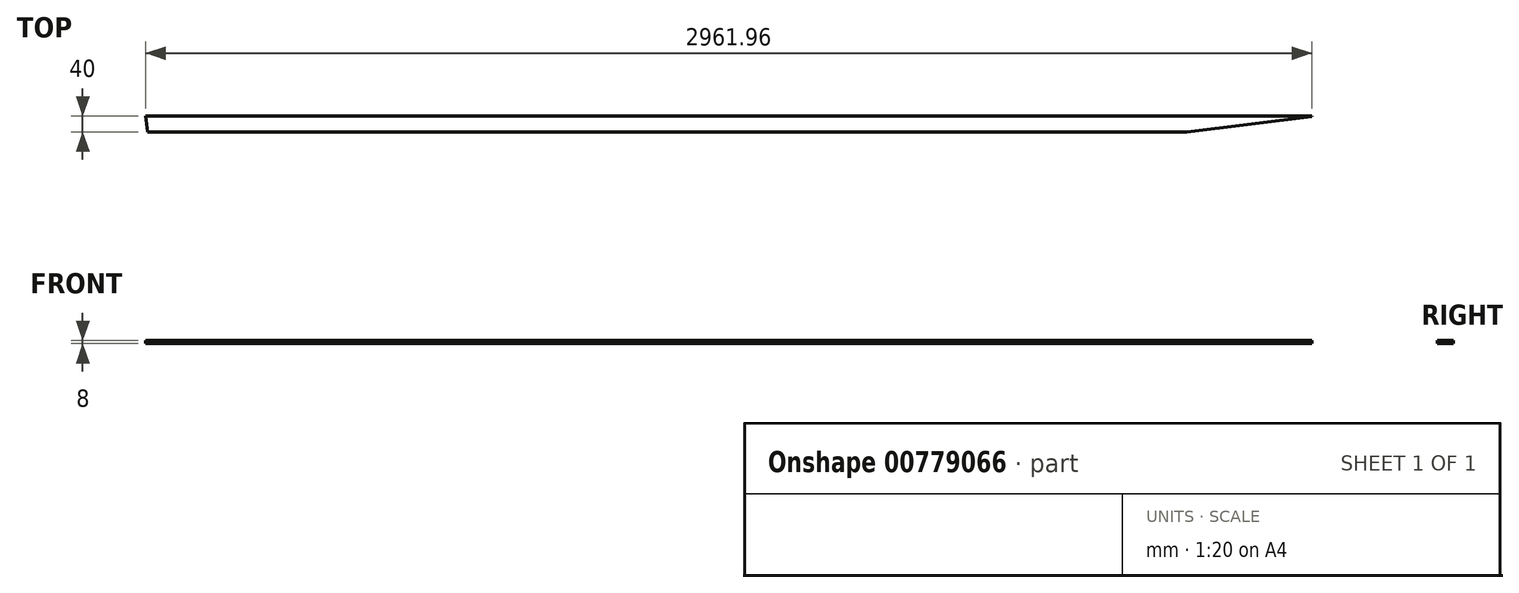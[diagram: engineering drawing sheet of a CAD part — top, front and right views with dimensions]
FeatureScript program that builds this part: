
annotation { "Feature Type Name" : "Feature", "Feature Type Description" : "" }
export const myFeature = defineFeature(function(context is Context, id is Id, definition is map)
    precondition{}
    {
        {
            var Q0;
            Q0=qCreatedBy(makeId("Top.planeOp"),FACE);
            var sketch = newSketch(context, id + "F0", { "sketchPlane" : qUnion([Q0])});
            skLineSegment(sketch, "E0.bottom", {"start": v(-1485.98, 20) * mm, "end": v(1485.98, 20) * mm});
            skLineSegment(sketch, "E0.top", {"start": v(-1485.98, -20) * mm, "end": v(1485.98, -20) * mm});
            skLineSegment(sketch, "E0.left", {"start": v(-1485.98, 20) * mm, "end": v(-1485.98, -20) * mm});
            skLineSegment(sketch, "E0.right", {"start": v(1485.98, 20) * mm, "end": v(1485.98, -20) * mm});
            skPoint(sketch, "E0.middle", {"position": v(0, 0) * mm});
            skSolve(sketch);
        }
        {
            var Q0;
            Q0=makeQuery(id+"F0.imprint","IMPRINT",FACE,{"disambiguationData":[TD([[makeQuery(id+"F0.imprint","IMPRINT",EDGE,{"derivedFrom":sQuery(id+"F0.wireOp",EDGE,"E0.bottom")}),-1.0]])]});
            extrude(context, id + "F1", {"entities" : qUnion([Q0]), "depth" : 8 * mm, "offsetDistance" : 25 * mm});
        }
        {
            var Q0;
            Q0=makeQuery(id+"F1.opExtrude","CAP_FACE",FACE,{"disambiguationData":[OSD([sQuery(id+"F0.wireOp",EDGE,"E0.bottom"),sQuery(id+"F0.wireOp",EDGE,"E0.top"),sQuery(id+"F0.wireOp",EDGE,"E0.left"),sQuery(id+"F0.wireOp",EDGE,"E0.right")])],"isStart":false});
            var sketch = newSketch(context, id + "F2", { "sketchPlane" : qUnion([Q0])});
            skLineSegment(sketch, "E1", {"start": v(1485.98, 20) * mm, "end": v(1159.31, -20) * mm});
            skSolve(sketch);
        }
        {
            var Q0;
            {var subQ0=sQuery(id+"F2.wireOp",EDGE,"E1");Q0=makeQuery(id+"F2.imprint","IMPRINT",FACE,{"disambiguationData":[TD([[makeQuery(id+"F2.imprint","IMPRINT",EDGE,{"derivedFrom":subQ0}),1.0]])]});}
            extrude(context, id + "F3", {"entities" : qUnion([Q0]), "operationType" : NewBodyOperationType.REMOVE, "oppositeDirection" : true, "depth" : 100 * mm, "offsetDistance" : 25 * mm});
        }
        {
            var Q0;
            Q0=makeQuery(id+"F1.opExtrude","CAP_FACE",FACE,{"disambiguationData":[OSD([sQuery(id+"F0.wireOp",EDGE,"E0.bottom"),sQuery(id+"F0.wireOp",EDGE,"E0.top"),sQuery(id+"F0.wireOp",EDGE,"E0.left"),sQuery(id+"F0.wireOp",EDGE,"E0.right")])],"isStart":false});
            var sketch = newSketch(context, id + "F4", { "sketchPlane" : qUnion([Q0])});
            skLineSegment(sketch, "E2", {"start": v(1485.98, 20) * mm, "end": v(1475.98, 20) * mm});
            skLineSegment(sketch, "E3", {"start": v(1475.98, 20) * mm, "end": v(1475.98, 18.78) * mm});
            skLineSegment(sketch, "E4", {"start": v(1475.98, 18.78) * mm, "end": v(1485.98, 20) * mm});
            skSolve(sketch);
        }
        {
            var Q0;
            Q0=makeQuery(id+"F4.imprint","IMPRINT",FACE,{"disambiguationData":[TD([[makeQuery(id+"F4.imprint","IMPRINT",EDGE,{"derivedFrom":sQuery(id+"F4.wireOp",EDGE,"E2")}),-1.0]])]});
            extrude(context, id + "F5", {"entities" : qUnion([Q0]), "operationType" : NewBodyOperationType.REMOVE, "oppositeDirection" : true, "depth" : 25 * mm, "offsetDistance" : 25 * mm});
        }
        {
            var Q0;
            Q0=makeQuery(id+"F1.opExtrude","CAP_FACE",FACE,{"disambiguationData":[OSD([sQuery(id+"F0.wireOp",EDGE,"E0.bottom"),sQuery(id+"F0.wireOp",EDGE,"E0.top"),sQuery(id+"F0.wireOp",EDGE,"E0.left"),sQuery(id+"F0.wireOp",EDGE,"E0.right")])],"isStart":false});
            var sketch = newSketch(context, id + "F6", { "sketchPlane" : qUnion([Q0])});
            skLineSegment(sketch, "E5", {"start": v(-1485.98, 20) * mm, "end": v(-1481.08, -20) * mm});
            skSolve(sketch);
        }
        {
            var Q0;
            {var subQ0=sQuery(id+"F6.wireOp",EDGE,"E5");Q0=makeQuery(id+"F6.imprint","IMPRINT",FACE,{"disambiguationData":[TD([[makeQuery(id+"F6.imprint","IMPRINT",EDGE,{"derivedFrom":subQ0}),-1.0]])]});}
            extrude(context, id + "F7", {"entities" : qUnion([Q0]), "operationType" : NewBodyOperationType.REMOVE, "oppositeDirection" : true, "depth" : 25 * mm, "offsetDistance" : 25 * mm});
        }
    });
